# Revit family: 1880034
name_source: partatom
category: Pipe Accessories
units: mm (PartAtom-declared; Revit-internal decimal feet)

## family parameters
Always vertical = Yes
Cut with Voids When Loaded = No
OmniClass Number = 23.45.00.00
OmniClass Title = Sanitary, Laundry, and Cleaning Equipment
Part Type = Valve - Breaks Into
Round Connector Dimension = Use Diameter
Shared = No
Work Plane-Based = No

## types (1)
- 1880034
    A = 161 mm
    B = 107 mm
    C = 80 mm
    CH = 29 mm
    D = 63 mm
    DN = 20 mm  [stored 0.0656168 ft]
    Description = MAGNETIC COMPACT DIRT SEPRATOR I-MAG
    E = 15 mm  [stored 0.0492126 ft]
    F = 39 mm
    G = 41 mm
    LBS-psi = 43.5
    Manufacturer = ITAP S.p.A.
    Matarial = Stainless steel AISI 304 cartridge
    Maximum working pressure = 3 bar
    Maximum working temperature = 90°C
    Model = 188
    Threads = ISO 228 (equivalent to DIN EN ISO 228 and BS EN ISO 228
    URL = https://www.itap.it
    kg/cm2 bar = 3

note: [stored X ft] marks values corroborated as IEEE doubles in the binary element streams (Revit-internal decimal feet)

## geometry (parser evidence)
native form markers: Sweep x3
no freeform markers — native parametric forms only
